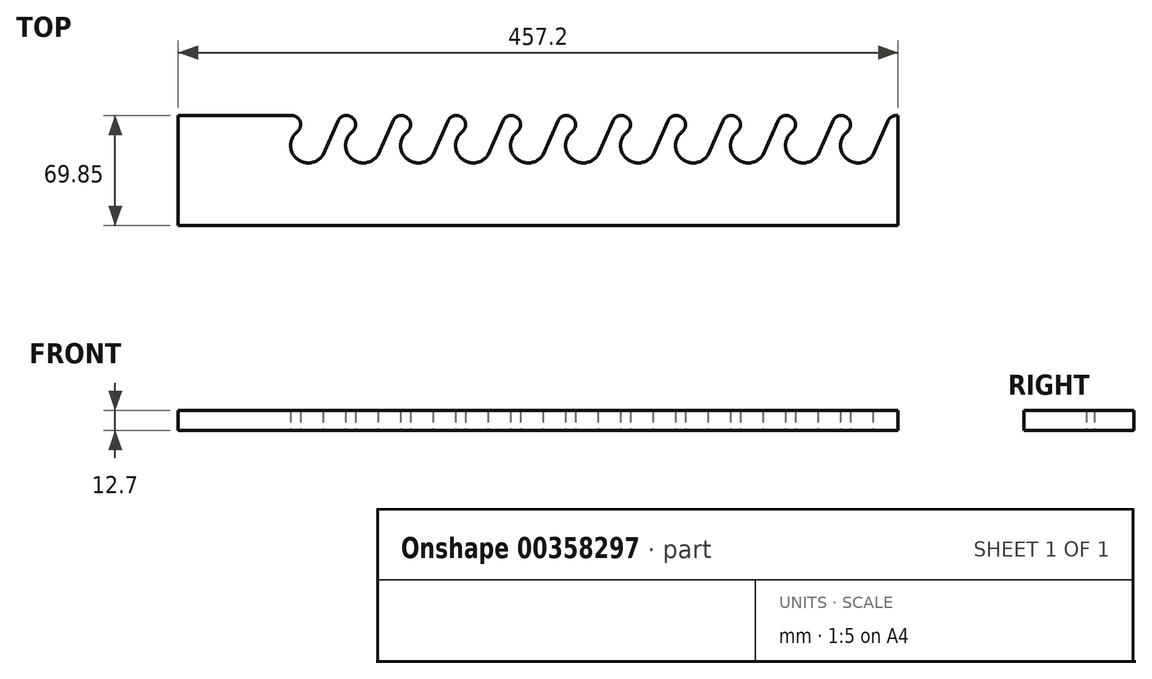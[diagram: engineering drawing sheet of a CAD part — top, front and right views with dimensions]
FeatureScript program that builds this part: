
annotation { "Feature Type Name" : "Feature", "Feature Type Description" : "" }
export const myFeature = defineFeature(function(context is Context, id is Id, definition is map)
    precondition{}
    {
        {
            var Q0;
            Q0=qCreatedBy(makeId("Top.planeOp"),FACE);
            var sketch = newSketch(context, id + "F0", { "sketchPlane" : qUnion([Q0])});
            skLineSegment(sketch, "E0.bottom", {"start": v(0, 0) * mm, "end": v(457.2, 0) * mm});
            skLineSegment(sketch, "E0.top", {"start": v(0, -69.85) * mm, "end": v(457.2, -69.85) * mm});
            skLineSegment(sketch, "E0.left", {"start": v(0, -69.85) * mm, "end": v(0, 0) * mm});
            skLineSegment(sketch, "E0.right", {"start": v(457.2, -69.85) * mm, "end": v(457.2, 0) * mm});
            skSolve(sketch);
        }
        {
            var Q0;
            Q0 = qSketchRegion(id + "F0", true);
            extrude(context, id + "F1", {"entities" : qUnion([Q0]), "depth" : 12.7 * mm});
        }
        {
            var Q0;
            Q0=qCreatedBy(makeId("Top.planeOp"),FACE);
            var sketch = newSketch(context, id + "F2", { "sketchPlane" : qUnion([Q0])});
            skLineSegment(sketch, "E1.bottom", {"start": v(0, 0) * mm, "end": v(71.92, 0) * mm});
            skLineSegment(sketch, "E1.left", {"start": v(0, 0) * mm, "end": v(0, -69.85) * mm});
            skArc(sketch, "E2", {"start": v(424.83, -10.4) * mm, "mid": v(424.36, -27.3) * mm, "end": v(441.14, -25.08) * mm});
            skArc(sketch, "E3", {"start": v(424.83, -10.4) * mm, "mid": v(426.68, -3.9) * mm, "end": v(421.17, 0) * mm});
            skLineSegment(sketch, "E4", {"start": v(450.76, -3.47) * mm, "end": v(441.14, -25.08) * mm});
            skArc(sketch, "E5", {"start": v(456.1, 0) * mm, "mid": v(452.91, -0.94) * mm, "end": v(450.76, -3.47) * mm});
            skLineSegment(sketch, "E6.direction1", {"start": v(431.8, -19.05) * mm, "end": v(466.73, -19.05) * mm, "construction": true});
            skLineSegment(sketch, "E7", {"start": v(421.17, 0) * mm, "end": v(421.17, 5.06) * mm});
            skLineSegment(sketch, "E8", {"start": v(421.17, 5.06) * mm, "end": v(456.1, 5.06) * mm});
            skLineSegment(sketch, "E9", {"start": v(456.1, 5.06) * mm, "end": v(456.1, 0) * mm});
            skLineSegment(sketch, "E10.1.0.0", {"start": v(386.24, 0) * mm, "end": v(386.24, 5.06) * mm});
            skLineSegment(sketch, "E10.1.0.1", {"start": v(415.83, -3.47) * mm, "end": v(406.21, -25.08) * mm});
            skArc(sketch, "E10.1.0.2", {"start": v(389.9, -10.4) * mm, "mid": v(391.75, -3.9) * mm, "end": v(386.24, 0) * mm});
            skLineSegment(sketch, "E10.1.0.3", {"start": v(386.24, 5.06) * mm, "end": v(421.17, 5.06) * mm});
            skArc(sketch, "E10.1.0.4", {"start": v(421.17, 0) * mm, "mid": v(417.99, -0.94) * mm, "end": v(415.83, -3.47) * mm});
            skArc(sketch, "E10.1.0.5", {"start": v(389.9, -10.4) * mm, "mid": v(389.44, -27.3) * mm, "end": v(406.21, -25.08) * mm});
            skLineSegment(sketch, "E10.1.0.6", {"start": v(421.17, 5.06) * mm, "end": v(421.17, 0) * mm});
            skLineSegment(sketch, "E10.1.0.7", {"start": v(396.88, -19.05) * mm, "end": v(431.8, -19.05) * mm, "construction": true});
            skLineSegment(sketch, "E10.2.0.0", {"start": v(351.32, 0) * mm, "end": v(351.32, 5.06) * mm});
            skLineSegment(sketch, "E10.2.0.1", {"start": v(380.9, -3.47) * mm, "end": v(371.29, -25.08) * mm});
            skArc(sketch, "E10.2.0.2", {"start": v(354.98, -10.4) * mm, "mid": v(356.83, -3.9) * mm, "end": v(351.32, 0) * mm});
            skLineSegment(sketch, "E10.2.0.3", {"start": v(351.32, 5.06) * mm, "end": v(386.24, 5.06) * mm});
            skArc(sketch, "E10.2.0.4", {"start": v(386.24, 0) * mm, "mid": v(383.06, -0.94) * mm, "end": v(380.9, -3.47) * mm});
            skArc(sketch, "E10.2.0.5", {"start": v(354.98, -10.4) * mm, "mid": v(354.51, -27.3) * mm, "end": v(371.29, -25.08) * mm});
            skLineSegment(sketch, "E10.2.0.6", {"start": v(386.24, 5.06) * mm, "end": v(386.24, 0) * mm});
            skLineSegment(sketch, "E10.2.0.7", {"start": v(361.95, -19.05) * mm, "end": v(396.88, -19.05) * mm, "construction": true});
            skLineSegment(sketch, "E10.3.0.0", {"start": v(316.4, 0) * mm, "end": v(316.4, 5.06) * mm});
            skLineSegment(sketch, "E10.3.0.1", {"start": v(345.98, -3.47) * mm, "end": v(336.36, -25.08) * mm});
            skArc(sketch, "E10.3.0.2", {"start": v(320.06, -10.4) * mm, "mid": v(321.9, -3.9) * mm, "end": v(316.4, 0) * mm});
            skLineSegment(sketch, "E10.3.0.3", {"start": v(316.4, 5.06) * mm, "end": v(351.32, 5.06) * mm});
            skArc(sketch, "E10.3.0.4", {"start": v(351.32, 0) * mm, "mid": v(348.14, -0.94) * mm, "end": v(345.98, -3.47) * mm});
            skArc(sketch, "E10.3.0.5", {"start": v(320.06, -10.4) * mm, "mid": v(319.59, -27.3) * mm, "end": v(336.36, -25.08) * mm});
            skLineSegment(sketch, "E10.3.0.6", {"start": v(351.32, 5.06) * mm, "end": v(351.32, 0) * mm});
            skLineSegment(sketch, "E10.3.0.7", {"start": v(327.03, -19.05) * mm, "end": v(361.95, -19.05) * mm, "construction": true});
            skLineSegment(sketch, "E10.4.0.0", {"start": v(281.47, 0) * mm, "end": v(281.47, 5.06) * mm});
            skLineSegment(sketch, "E10.4.0.1", {"start": v(311.06, -3.47) * mm, "end": v(301.44, -25.08) * mm});
            skArc(sketch, "E10.4.0.2", {"start": v(285.13, -10.4) * mm, "mid": v(286.98, -3.9) * mm, "end": v(281.47, 0) * mm});
            skLineSegment(sketch, "E10.4.0.3", {"start": v(281.47, 5.06) * mm, "end": v(316.4, 5.06) * mm});
            skArc(sketch, "E10.4.0.4", {"start": v(316.4, 0) * mm, "mid": v(313.21, -0.94) * mm, "end": v(311.06, -3.47) * mm});
            skArc(sketch, "E10.4.0.5", {"start": v(285.13, -10.4) * mm, "mid": v(284.66, -27.3) * mm, "end": v(301.44, -25.08) * mm});
            skLineSegment(sketch, "E10.4.0.6", {"start": v(316.4, 5.06) * mm, "end": v(316.4, 0) * mm});
            skLineSegment(sketch, "E10.4.0.7", {"start": v(292.1, -19.05) * mm, "end": v(327.03, -19.05) * mm, "construction": true});
            skLineSegment(sketch, "E10.5.0.0", {"start": v(246.54, 0) * mm, "end": v(246.54, 5.06) * mm});
            skLineSegment(sketch, "E10.5.0.1", {"start": v(276.13, -3.47) * mm, "end": v(266.51, -25.08) * mm});
            skArc(sketch, "E10.5.0.2", {"start": v(250.2, -10.4) * mm, "mid": v(252.05, -3.9) * mm, "end": v(246.54, 0) * mm});
            skLineSegment(sketch, "E10.5.0.3", {"start": v(246.54, 5.06) * mm, "end": v(281.47, 5.06) * mm});
            skArc(sketch, "E10.5.0.4", {"start": v(281.47, 0) * mm, "mid": v(278.29, -0.94) * mm, "end": v(276.13, -3.47) * mm});
            skArc(sketch, "E10.5.0.5", {"start": v(250.2, -10.4) * mm, "mid": v(249.74, -27.3) * mm, "end": v(266.51, -25.08) * mm});
            skLineSegment(sketch, "E10.5.0.6", {"start": v(281.47, 5.06) * mm, "end": v(281.47, 0) * mm});
            skLineSegment(sketch, "E10.5.0.7", {"start": v(257.18, -19.05) * mm, "end": v(292.1, -19.05) * mm, "construction": true});
            skLineSegment(sketch, "E10.6.0.0", {"start": v(211.62, 0) * mm, "end": v(211.62, 5.06) * mm});
            skLineSegment(sketch, "E10.6.0.1", {"start": v(241.2, -3.47) * mm, "end": v(231.59, -25.08) * mm});
            skArc(sketch, "E10.6.0.2", {"start": v(215.28, -10.4) * mm, "mid": v(217.13, -3.9) * mm, "end": v(211.62, 0) * mm});
            skLineSegment(sketch, "E10.6.0.3", {"start": v(211.62, 5.06) * mm, "end": v(246.54, 5.06) * mm});
            skArc(sketch, "E10.6.0.4", {"start": v(246.54, 0) * mm, "mid": v(243.36, -0.94) * mm, "end": v(241.2, -3.47) * mm});
            skArc(sketch, "E10.6.0.5", {"start": v(215.28, -10.4) * mm, "mid": v(214.81, -27.3) * mm, "end": v(231.59, -25.08) * mm});
            skLineSegment(sketch, "E10.6.0.6", {"start": v(246.54, 5.06) * mm, "end": v(246.54, 0) * mm});
            skLineSegment(sketch, "E10.6.0.7", {"start": v(222.25, -19.05) * mm, "end": v(257.18, -19.05) * mm, "construction": true});
            skLineSegment(sketch, "E10.7.0.0", {"start": v(176.7, 0) * mm, "end": v(176.7, 5.06) * mm});
            skLineSegment(sketch, "E10.7.0.1", {"start": v(206.28, -3.47) * mm, "end": v(196.66, -25.08) * mm});
            skArc(sketch, "E10.7.0.2", {"start": v(180.36, -10.4) * mm, "mid": v(182.2, -3.9) * mm, "end": v(176.7, 0) * mm});
            skLineSegment(sketch, "E10.7.0.3", {"start": v(176.7, 5.06) * mm, "end": v(211.62, 5.06) * mm});
            skArc(sketch, "E10.7.0.4", {"start": v(211.62, 0) * mm, "mid": v(208.44, -0.94) * mm, "end": v(206.28, -3.47) * mm});
            skArc(sketch, "E10.7.0.5", {"start": v(180.36, -10.4) * mm, "mid": v(179.89, -27.3) * mm, "end": v(196.66, -25.08) * mm});
            skLineSegment(sketch, "E10.7.0.6", {"start": v(211.62, 5.06) * mm, "end": v(211.62, 0) * mm});
            skLineSegment(sketch, "E10.7.0.7", {"start": v(187.33, -19.05) * mm, "end": v(222.25, -19.05) * mm, "construction": true});
            skLineSegment(sketch, "E10.8.0.0", {"start": v(141.77, 0) * mm, "end": v(141.77, 5.06) * mm});
            skLineSegment(sketch, "E10.8.0.1", {"start": v(171.36, -3.47) * mm, "end": v(161.74, -25.08) * mm});
            skArc(sketch, "E10.8.0.2", {"start": v(145.43, -10.4) * mm, "mid": v(147.28, -3.9) * mm, "end": v(141.77, 0) * mm});
            skLineSegment(sketch, "E10.8.0.3", {"start": v(141.77, 5.06) * mm, "end": v(176.7, 5.06) * mm});
            skArc(sketch, "E10.8.0.4", {"start": v(176.7, 0) * mm, "mid": v(173.51, -0.94) * mm, "end": v(171.36, -3.47) * mm});
            skArc(sketch, "E10.8.0.5", {"start": v(145.43, -10.4) * mm, "mid": v(144.96, -27.3) * mm, "end": v(161.74, -25.08) * mm});
            skLineSegment(sketch, "E10.8.0.6", {"start": v(176.7, 5.06) * mm, "end": v(176.7, 0) * mm});
            skLineSegment(sketch, "E10.8.0.7", {"start": v(152.4, -19.05) * mm, "end": v(187.33, -19.05) * mm, "construction": true});
            skLineSegment(sketch, "E10.9.0.0", {"start": v(106.84, 0) * mm, "end": v(106.84, 5.06) * mm});
            skLineSegment(sketch, "E10.9.0.1", {"start": v(136.43, -3.47) * mm, "end": v(126.81, -25.08) * mm});
            skArc(sketch, "E10.9.0.2", {"start": v(110.5, -10.4) * mm, "mid": v(112.35, -3.9) * mm, "end": v(106.84, 0) * mm});
            skLineSegment(sketch, "E10.9.0.3", {"start": v(106.84, 5.06) * mm, "end": v(141.77, 5.06) * mm});
            skArc(sketch, "E10.9.0.4", {"start": v(141.77, 0) * mm, "mid": v(138.59, -0.94) * mm, "end": v(136.43, -3.47) * mm});
            skArc(sketch, "E10.9.0.5", {"start": v(110.5, -10.4) * mm, "mid": v(110.04, -27.3) * mm, "end": v(126.81, -25.08) * mm});
            skLineSegment(sketch, "E10.9.0.6", {"start": v(141.77, 5.06) * mm, "end": v(141.77, 0) * mm});
            skLineSegment(sketch, "E10.9.0.7", {"start": v(117.48, -19.05) * mm, "end": v(152.4, -19.05) * mm, "construction": true});
            skLineSegment(sketch, "E10.10.0.0", {"start": v(71.92, 0) * mm, "end": v(71.92, 5.06) * mm});
            skLineSegment(sketch, "E10.10.0.1", {"start": v(101.5, -3.47) * mm, "end": v(91.89, -25.08) * mm});
            skArc(sketch, "E10.10.0.2", {"start": v(75.58, -10.4) * mm, "mid": v(77.43, -3.9) * mm, "end": v(71.92, 0) * mm});
            skLineSegment(sketch, "E10.10.0.3", {"start": v(71.92, 5.06) * mm, "end": v(106.84, 5.06) * mm});
            skArc(sketch, "E10.10.0.4", {"start": v(106.84, 0) * mm, "mid": v(103.66, -0.94) * mm, "end": v(101.5, -3.47) * mm});
            skArc(sketch, "E10.10.0.5", {"start": v(75.58, -10.4) * mm, "mid": v(75.11, -27.3) * mm, "end": v(91.89, -25.08) * mm});
            skLineSegment(sketch, "E10.10.0.6", {"start": v(106.84, 5.06) * mm, "end": v(106.84, 0) * mm});
            skLineSegment(sketch, "E10.10.0.7", {"start": v(82.55, -19.05) * mm, "end": v(117.48, -19.05) * mm, "construction": true});
            skLineSegment(sketch, "E10.direction1", {"start": v(431.8, -19.05) * mm, "end": v(396.88, -19.05) * mm, "construction": true});
            skSolve(sketch);
        }
        {
            var Q0;
            Q0 = qSketchRegion(id + "F2", true);
            extrude(context, id + "F3", {"entities" : qUnion([Q0]), "operationType" : NewBodyOperationType.REMOVE, "depth" : 25.4 * mm});
        }
    });
